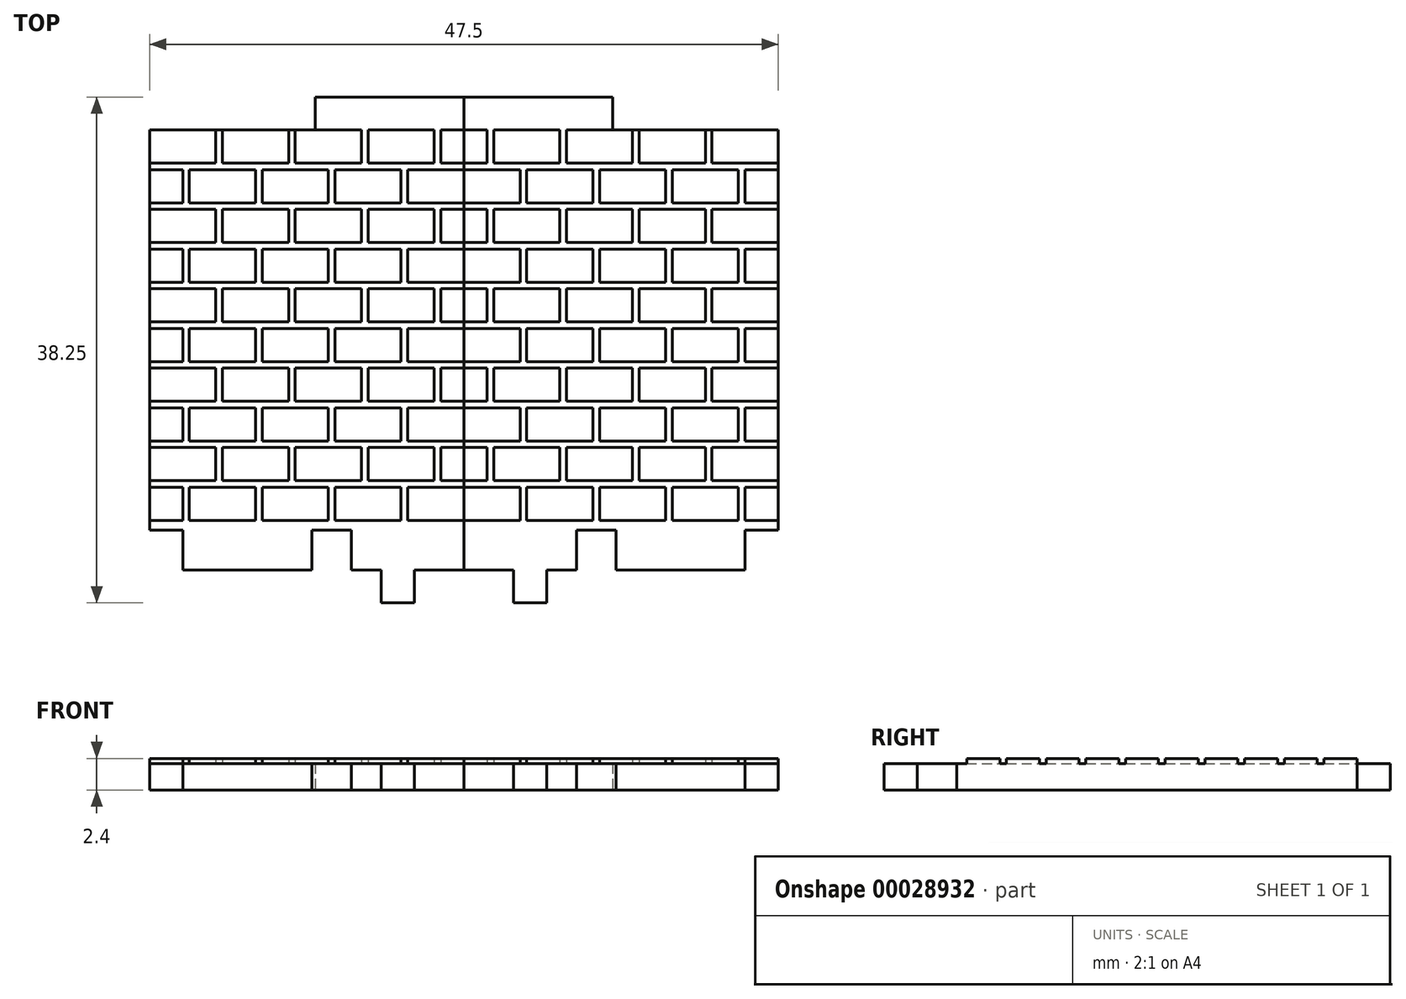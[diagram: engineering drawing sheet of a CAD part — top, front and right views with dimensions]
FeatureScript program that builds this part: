
annotation { "Feature Type Name" : "Feature", "Feature Type Description" : "" }
export const myFeature = defineFeature(function(context is Context, id is Id, definition is map)
    precondition{}
    {
        {
            var Q0;
            Q0=qCreatedBy(makeId("Top.planeOp"),FACE);
            var sketch = newSketch(context, id + "F0", { "sketchPlane" : qUnion([Q0])});
            skLineSegment(sketch, "E0.bottom", {"start": v(-8.5, -5.78) * mm, "end": v(-11.5, -5.78) * mm});
            skLineSegment(sketch, "E0.top", {"start": v(-11.25, 24.47) * mm, "end": v(-23.75, 24.47) * mm});
            skLineSegment(sketch, "E0.right", {"start": v(-23.75, -5.78) * mm, "end": v(-23.75, 24.47) * mm});
            skLineSegment(sketch, "E1.top", {"start": v(-11.25, 26.97) * mm, "end": v(0, 26.97) * mm});
            skLineSegment(sketch, "E1.left", {"start": v(-11.25, 24.47) * mm, "end": v(-11.25, 26.97) * mm});
            skLineSegment(sketch, "E1.right", {"start": v(0, -8.78) * mm, "end": v(0, 26.97) * mm});
            skLineSegment(sketch, "E2.top", {"start": v(-21.25, -8.78) * mm, "end": v(-11.5, -8.78) * mm});
            skLineSegment(sketch, "E2.left", {"start": v(-21.25, -5.78) * mm, "end": v(-21.25, -8.78) * mm});
            skLineSegment(sketch, "E2.right", {"start": v(-11.5, -5.78) * mm, "end": v(-11.5, -8.78) * mm});
            skLineSegment(sketch, "E3.top", {"start": v(-8.5, -8.78) * mm, "end": v(-6.25, -8.78) * mm});
            skLineSegment(sketch, "E3.left", {"start": v(-8.5, -5.78) * mm, "end": v(-8.5, -8.78) * mm});
            skLineSegment(sketch, "E4.top", {"start": v(-6.25, -11.28) * mm, "end": v(-3.75, -11.28) * mm});
            skLineSegment(sketch, "E4.left", {"start": v(-6.25, -8.78) * mm, "end": v(-6.25, -11.28) * mm});
            skLineSegment(sketch, "E4.right", {"start": v(-3.75, -8.78) * mm, "end": v(-3.75, -11.28) * mm});
            skLineSegment(sketch, "E5.trimOffspring", {"start": v(-3.75, -8.78) * mm, "end": v(0, -8.78) * mm});
            skLineSegment(sketch, "E6.trimOffspring", {"start": v(-21.25, -5.78) * mm, "end": v(-23.75, -5.78) * mm});
            skLineSegment(sketch, "E7.MirrorCS", {"start": v(11.25, 26.97) * mm, "end": v(0, 26.97) * mm});
            skLineSegment(sketch, "E8.MirrorCS", {"start": v(11.25, 24.47) * mm, "end": v(11.25, 26.97) * mm});
            skLineSegment(sketch, "E9.MirrorCS", {"start": v(11.25, 24.47) * mm, "end": v(23.75, 24.47) * mm});
            skLineSegment(sketch, "E10.MirrorCS", {"start": v(23.75, -5.78) * mm, "end": v(23.75, 24.47) * mm});
            skLineSegment(sketch, "E11.MirrorCS", {"start": v(21.25, -5.78) * mm, "end": v(23.75, -5.78) * mm});
            skLineSegment(sketch, "E12.MirrorCS", {"start": v(21.25, -5.78) * mm, "end": v(21.25, -8.78) * mm});
            skLineSegment(sketch, "E13.MirrorCS", {"start": v(21.25, -8.78) * mm, "end": v(11.5, -8.78) * mm});
            skLineSegment(sketch, "E14.MirrorCS", {"start": v(11.5, -5.78) * mm, "end": v(11.5, -8.78) * mm});
            skLineSegment(sketch, "E15.MirrorCS", {"start": v(8.5, -5.78) * mm, "end": v(11.5, -5.78) * mm});
            skLineSegment(sketch, "E16.MirrorCS", {"start": v(8.5, -5.78) * mm, "end": v(8.5, -8.78) * mm});
            skLineSegment(sketch, "E17.MirrorCS", {"start": v(8.5, -8.78) * mm, "end": v(6.25, -8.78) * mm});
            skLineSegment(sketch, "E18.MirrorCS", {"start": v(6.25, -8.78) * mm, "end": v(6.25, -11.28) * mm});
            skLineSegment(sketch, "E19.MirrorCS", {"start": v(6.25, -11.28) * mm, "end": v(3.75, -11.28) * mm});
            skLineSegment(sketch, "E20.MirrorCS", {"start": v(3.75, -8.78) * mm, "end": v(3.75, -11.28) * mm});
            skLineSegment(sketch, "E21.MirrorCS", {"start": v(3.75, -8.78) * mm, "end": v(0, -8.78) * mm});
            skSolve(sketch);
        }
        {
            var Q0;
            Q0=makeQuery(id+"F0.imprint","IMPRINT",FACE,{"disambiguationData":[TD([[makeQuery(id+"F0.imprint","IMPRINT",EDGE,{"derivedFrom":sQuery(id+"F0.wireOp",EDGE,"E0.bottom")}),-1.0]])]});
            extrude(context, id + "F1", {"entities" : qUnion([Q0]), "depth" : 2 * mm});
        }
        {
            var Q0;
            Q0=makeQuery(id+"F1.opExtrude","CAP_FACE",FACE,{"disambiguationData":[OSD([sQuery(id+"F0.wireOp",EDGE,"E0.bottom"),sQuery(id+"F0.wireOp",EDGE,"E0.top"),sQuery(id+"F0.wireOp",EDGE,"E0.right"),sQuery(id+"F0.wireOp",EDGE,"E1.top"),sQuery(id+"F0.wireOp",EDGE,"E1.left"),sQuery(id+"F0.wireOp",EDGE,"E1.right"),sQuery(id+"F0.wireOp",EDGE,"E2.top"),sQuery(id+"F0.wireOp",EDGE,"E2.left"),sQuery(id+"F0.wireOp",EDGE,"E2.right"),sQuery(id+"F0.wireOp",EDGE,"E3.top"),sQuery(id+"F0.wireOp",EDGE,"E3.left"),sQuery(id+"F0.wireOp",EDGE,"E4.top"),sQuery(id+"F0.wireOp",EDGE,"E4.left"),sQuery(id+"F0.wireOp",EDGE,"E4.right"),sQuery(id+"F0.wireOp",EDGE,"E5.trimOffspring"),sQuery(id+"F0.wireOp",EDGE,"E6.trimOffspring")])],"isStart":false});
            var sketch = newSketch(context, id + "F2", { "sketchPlane" : qUnion([Q0])});
            skLineSegment(sketch, "E22", {"start": v(-23.75, 21.97) * mm, "end": v(0, 21.97) * mm});
            skLineSegment(sketch, "E23", {"start": v(-23.75, 24.47) * mm, "end": v(0, 24.47) * mm});
            skLineSegment(sketch, "E24", {"start": v(-18.75, 24.47) * mm, "end": v(-18.75, 21.97) * mm});
            skLineSegment(sketch, "E25", {"start": v(-18.25, 21.97) * mm, "end": v(-18.25, 24.47) * mm});
            skLineSegment(sketch, "E26.1.0.0", {"start": v(-13.25, 24.47) * mm, "end": v(-13.25, 21.97) * mm});
            skLineSegment(sketch, "E26.1.0.1", {"start": v(-12.75, 21.97) * mm, "end": v(-12.75, 24.47) * mm});
            skLineSegment(sketch, "E26.2.0.0", {"start": v(-7.75, 24.47) * mm, "end": v(-7.75, 21.97) * mm});
            skLineSegment(sketch, "E26.2.0.1", {"start": v(-7.25, 21.97) * mm, "end": v(-7.25, 24.47) * mm});
            skLineSegment(sketch, "E26.3.0.0", {"start": v(-2.25, 24.47) * mm, "end": v(-2.25, 21.97) * mm});
            skLineSegment(sketch, "E26.3.0.1", {"start": v(-1.75, 21.97) * mm, "end": v(-1.75, 24.47) * mm});
            skLineSegment(sketch, "E26.direction1", {"start": v(-18.75, 21.97) * mm, "end": v(-13.25, 21.97) * mm, "construction": true});
            skLineSegment(sketch, "E27", {"start": v(0, 24.47) * mm, "end": v(4, 24.47) * mm});
            skLineSegment(sketch, "E28", {"start": v(0, 21.97) * mm, "end": v(4, 21.97) * mm});
            skLineSegment(sketch, "E29.1.0.0", {"start": v(-26.25, 21.47) * mm, "end": v(-2.5, 21.47) * mm});
            skLineSegment(sketch, "E29.1.0.1", {"start": v(-2.5, 21.47) * mm, "end": v(1.5, 21.47) * mm});
            skLineSegment(sketch, "E29.1.0.2", {"start": v(-2.5, 18.97) * mm, "end": v(1.5, 18.97) * mm});
            skLineSegment(sketch, "E29.1.0.3", {"start": v(-26.25, 18.97) * mm, "end": v(-2.5, 18.97) * mm});
            skLineSegment(sketch, "E29.1.0.4", {"start": v(-4.25, 18.97) * mm, "end": v(-4.25, 21.47) * mm});
            skLineSegment(sketch, "E29.1.0.5", {"start": v(-4.75, 21.47) * mm, "end": v(-4.75, 18.97) * mm});
            skLineSegment(sketch, "E29.1.0.6", {"start": v(-9.75, 18.97) * mm, "end": v(-9.75, 21.47) * mm});
            skLineSegment(sketch, "E29.1.0.7", {"start": v(-10.25, 21.47) * mm, "end": v(-10.25, 18.97) * mm});
            skLineSegment(sketch, "E29.1.0.8", {"start": v(-15.25, 18.97) * mm, "end": v(-15.25, 21.47) * mm});
            skLineSegment(sketch, "E29.1.0.9", {"start": v(-15.75, 21.47) * mm, "end": v(-15.75, 18.97) * mm});
            skLineSegment(sketch, "E29.1.0.10", {"start": v(-20.75, 18.97) * mm, "end": v(-20.75, 21.47) * mm});
            skLineSegment(sketch, "E29.1.0.11", {"start": v(-21.25, 21.47) * mm, "end": v(-21.25, 18.97) * mm});
            skLineSegment(sketch, "E29.direction1", {"start": v(-23.75, 24.47) * mm, "end": v(-26.25, 21.47) * mm, "construction": true});
            skLineSegment(sketch, "E30.0.1.0", {"start": v(-23.75, 18.47) * mm, "end": v(-26.25, 15.47) * mm, "construction": true});
            skLineSegment(sketch, "E30.0.1.1", {"start": v(-26.25, 12.97) * mm, "end": v(-2.5, 12.97) * mm});
            skLineSegment(sketch, "E30.0.1.2", {"start": v(-23.75, 18.47) * mm, "end": v(0, 18.47) * mm});
            skLineSegment(sketch, "E30.0.1.3", {"start": v(-2.5, 12.97) * mm, "end": v(1.5, 12.97) * mm});
            skLineSegment(sketch, "E30.0.1.4", {"start": v(-23.75, 15.97) * mm, "end": v(0, 15.97) * mm});
            skLineSegment(sketch, "E30.0.1.5", {"start": v(-26.25, 15.47) * mm, "end": v(-2.5, 15.47) * mm});
            skLineSegment(sketch, "E30.0.1.6", {"start": v(-13.25, 18.47) * mm, "end": v(-13.25, 15.97) * mm});
            skLineSegment(sketch, "E30.0.1.7", {"start": v(-4.25, 12.97) * mm, "end": v(-4.25, 15.47) * mm});
            skLineSegment(sketch, "E30.0.1.8", {"start": v(-1.75, 15.97) * mm, "end": v(-1.75, 18.47) * mm});
            skLineSegment(sketch, "E30.0.1.9", {"start": v(-4.75, 15.47) * mm, "end": v(-4.75, 12.97) * mm});
            skLineSegment(sketch, "E30.0.1.10", {"start": v(-7.25, 15.97) * mm, "end": v(-7.25, 18.47) * mm});
            skLineSegment(sketch, "E30.0.1.11", {"start": v(0, 15.97) * mm, "end": v(4, 15.97) * mm});
            skLineSegment(sketch, "E30.0.1.12", {"start": v(-9.75, 12.97) * mm, "end": v(-9.75, 15.47) * mm});
            skLineSegment(sketch, "E30.0.1.13", {"start": v(-15.75, 15.47) * mm, "end": v(-15.75, 12.97) * mm});
            skLineSegment(sketch, "E30.0.1.14", {"start": v(-10.25, 15.47) * mm, "end": v(-10.25, 12.97) * mm});
            skLineSegment(sketch, "E30.0.1.15", {"start": v(-2.25, 18.47) * mm, "end": v(-2.25, 15.97) * mm});
            skLineSegment(sketch, "E30.0.1.16", {"start": v(-20.75, 12.97) * mm, "end": v(-20.75, 15.47) * mm});
            skLineSegment(sketch, "E30.0.1.17", {"start": v(-18.75, 15.97) * mm, "end": v(-13.25, 15.97) * mm, "construction": true});
            skLineSegment(sketch, "E30.0.1.18", {"start": v(0, 18.47) * mm, "end": v(4, 18.47) * mm});
            skLineSegment(sketch, "E30.0.1.19", {"start": v(-7.75, 18.47) * mm, "end": v(-7.75, 15.97) * mm});
            skLineSegment(sketch, "E30.0.1.20", {"start": v(-18.75, 18.47) * mm, "end": v(-18.75, 15.97) * mm});
            skLineSegment(sketch, "E30.0.1.21", {"start": v(-18.25, 15.97) * mm, "end": v(-18.25, 18.47) * mm});
            skLineSegment(sketch, "E30.0.1.22", {"start": v(-21.25, 15.47) * mm, "end": v(-21.25, 12.97) * mm});
            skLineSegment(sketch, "E30.0.1.23", {"start": v(-12.75, 15.97) * mm, "end": v(-12.75, 18.47) * mm});
            skLineSegment(sketch, "E30.0.1.24", {"start": v(-15.25, 12.97) * mm, "end": v(-15.25, 15.47) * mm});
            skLineSegment(sketch, "E30.0.1.25", {"start": v(-2.5, 15.47) * mm, "end": v(1.5, 15.47) * mm});
            skLineSegment(sketch, "E30.direction1", {"start": v(-26.25, 21.47) * mm, "end": v(-1.25, 21.47) * mm, "construction": true});
            skLineSegment(sketch, "E30.direction2", {"start": v(-26.25, 21.47) * mm, "end": v(-26.25, 15.47) * mm, "construction": true});
            skLineSegment(sketch, "E31.0.0.2", {"start": v(-23.75, 12.47) * mm, "end": v(-26.25, 9.47) * mm, "construction": true});
            skLineSegment(sketch, "E31.3.0.2", {"start": v(-26.25, 6.97) * mm, "end": v(-2.5, 6.97) * mm});
            skLineSegment(sketch, "E31.6.0.2", {"start": v(-23.75, 12.47) * mm, "end": v(0, 12.47) * mm});
            skLineSegment(sketch, "E31.9.0.2", {"start": v(-2.5, 6.97) * mm, "end": v(1.5, 6.97) * mm});
            skLineSegment(sketch, "E31.12.0.2", {"start": v(-23.75, 9.97) * mm, "end": v(0, 9.97) * mm});
            skLineSegment(sketch, "E31.15.0.2", {"start": v(-26.25, 9.47) * mm, "end": v(-2.5, 9.47) * mm});
            skLineSegment(sketch, "E31.18.0.2", {"start": v(-13.25, 12.47) * mm, "end": v(-13.25, 9.97) * mm});
            skLineSegment(sketch, "E31.21.0.2", {"start": v(-4.25, 6.97) * mm, "end": v(-4.25, 9.47) * mm});
            skLineSegment(sketch, "E31.24.0.2", {"start": v(-1.75, 9.97) * mm, "end": v(-1.75, 12.47) * mm});
            skLineSegment(sketch, "E31.27.0.2", {"start": v(-4.75, 9.47) * mm, "end": v(-4.75, 6.97) * mm});
            skLineSegment(sketch, "E31.30.0.2", {"start": v(-7.25, 9.97) * mm, "end": v(-7.25, 12.47) * mm});
            skLineSegment(sketch, "E31.33.0.2", {"start": v(0, 9.97) * mm, "end": v(4, 9.97) * mm});
            skLineSegment(sketch, "E31.36.0.2", {"start": v(-9.75, 6.97) * mm, "end": v(-9.75, 9.47) * mm});
            skLineSegment(sketch, "E31.39.0.2", {"start": v(-15.75, 9.47) * mm, "end": v(-15.75, 6.97) * mm});
            skLineSegment(sketch, "E31.42.0.2", {"start": v(-10.25, 9.47) * mm, "end": v(-10.25, 6.97) * mm});
            skLineSegment(sketch, "E31.45.0.2", {"start": v(-2.25, 12.47) * mm, "end": v(-2.25, 9.97) * mm});
            skLineSegment(sketch, "E31.48.0.2", {"start": v(-20.75, 6.97) * mm, "end": v(-20.75, 9.47) * mm});
            skLineSegment(sketch, "E31.51.0.2", {"start": v(-18.75, 9.97) * mm, "end": v(-13.25, 9.97) * mm, "construction": true});
            skLineSegment(sketch, "E31.54.0.2", {"start": v(0, 12.47) * mm, "end": v(4, 12.47) * mm});
            skLineSegment(sketch, "E31.57.0.2", {"start": v(-7.75, 12.47) * mm, "end": v(-7.75, 9.97) * mm});
            skLineSegment(sketch, "E31.60.0.2", {"start": v(-18.75, 12.47) * mm, "end": v(-18.75, 9.97) * mm});
            skLineSegment(sketch, "E31.63.0.2", {"start": v(-18.25, 9.97) * mm, "end": v(-18.25, 12.47) * mm});
            skLineSegment(sketch, "E31.66.0.2", {"start": v(-21.25, 9.47) * mm, "end": v(-21.25, 6.97) * mm});
            skLineSegment(sketch, "E31.69.0.2", {"start": v(-12.75, 9.97) * mm, "end": v(-12.75, 12.47) * mm});
            skLineSegment(sketch, "E31.72.0.2", {"start": v(-15.25, 6.97) * mm, "end": v(-15.25, 9.47) * mm});
            skLineSegment(sketch, "E31.75.0.2", {"start": v(-2.5, 9.47) * mm, "end": v(1.5, 9.47) * mm});
            skLineSegment(sketch, "E32.0.0.3", {"start": v(-23.75, 6.47) * mm, "end": v(-26.25, 3.47) * mm, "construction": true});
            skLineSegment(sketch, "E32.3.0.3", {"start": v(-26.25, 0.97) * mm, "end": v(-2.5, 0.97) * mm});
            skLineSegment(sketch, "E32.6.0.3", {"start": v(-23.75, 6.47) * mm, "end": v(0, 6.47) * mm});
            skLineSegment(sketch, "E32.9.0.3", {"start": v(-2.5, 0.97) * mm, "end": v(1.5, 0.97) * mm});
            skLineSegment(sketch, "E32.12.0.3", {"start": v(-23.75, 3.97) * mm, "end": v(0, 3.97) * mm});
            skLineSegment(sketch, "E32.15.0.3", {"start": v(-26.25, 3.47) * mm, "end": v(-2.5, 3.47) * mm});
            skLineSegment(sketch, "E32.18.0.3", {"start": v(-13.25, 6.47) * mm, "end": v(-13.25, 3.97) * mm});
            skLineSegment(sketch, "E32.21.0.3", {"start": v(-4.25, 0.97) * mm, "end": v(-4.25, 3.47) * mm});
            skLineSegment(sketch, "E32.24.0.3", {"start": v(-1.75, 3.97) * mm, "end": v(-1.75, 6.47) * mm});
            skLineSegment(sketch, "E32.27.0.3", {"start": v(-4.75, 3.47) * mm, "end": v(-4.75, 0.97) * mm});
            skLineSegment(sketch, "E32.30.0.3", {"start": v(-7.25, 3.97) * mm, "end": v(-7.25, 6.47) * mm});
            skLineSegment(sketch, "E32.33.0.3", {"start": v(0, 3.97) * mm, "end": v(4, 3.97) * mm});
            skLineSegment(sketch, "E32.36.0.3", {"start": v(-9.75, 0.97) * mm, "end": v(-9.75, 3.47) * mm});
            skLineSegment(sketch, "E32.39.0.3", {"start": v(-15.75, 3.47) * mm, "end": v(-15.75, 0.97) * mm});
            skLineSegment(sketch, "E32.42.0.3", {"start": v(-10.25, 3.47) * mm, "end": v(-10.25, 0.97) * mm});
            skLineSegment(sketch, "E32.45.0.3", {"start": v(-2.25, 6.47) * mm, "end": v(-2.25, 3.97) * mm});
            skLineSegment(sketch, "E32.48.0.3", {"start": v(-20.75, 0.97) * mm, "end": v(-20.75, 3.47) * mm});
            skLineSegment(sketch, "E32.51.0.3", {"start": v(-18.75, 3.97) * mm, "end": v(-13.25, 3.97) * mm, "construction": true});
            skLineSegment(sketch, "E32.54.0.3", {"start": v(0, 6.47) * mm, "end": v(4, 6.47) * mm});
            skLineSegment(sketch, "E32.57.0.3", {"start": v(-7.75, 6.47) * mm, "end": v(-7.75, 3.97) * mm});
            skLineSegment(sketch, "E32.60.0.3", {"start": v(-18.75, 6.47) * mm, "end": v(-18.75, 3.97) * mm});
            skLineSegment(sketch, "E32.63.0.3", {"start": v(-18.25, 3.97) * mm, "end": v(-18.25, 6.47) * mm});
            skLineSegment(sketch, "E32.66.0.3", {"start": v(-21.25, 3.47) * mm, "end": v(-21.25, 0.97) * mm});
            skLineSegment(sketch, "E32.69.0.3", {"start": v(-12.75, 3.97) * mm, "end": v(-12.75, 6.47) * mm});
            skLineSegment(sketch, "E32.72.0.3", {"start": v(-15.25, 0.97) * mm, "end": v(-15.25, 3.47) * mm});
            skLineSegment(sketch, "E32.75.0.3", {"start": v(-2.5, 3.47) * mm, "end": v(1.5, 3.47) * mm});
            skLineSegment(sketch, "E32.0.0.4", {"start": v(-23.75, 0.47) * mm, "end": v(-26.25, -2.53) * mm, "construction": true});
            skLineSegment(sketch, "E32.3.0.4", {"start": v(-26.25, -5.03) * mm, "end": v(-2.5, -5.03) * mm});
            skLineSegment(sketch, "E32.6.0.4", {"start": v(-23.75, 0.47) * mm, "end": v(0, 0.47) * mm});
            skLineSegment(sketch, "E32.9.0.4", {"start": v(-2.5, -5.03) * mm, "end": v(1.5, -5.03) * mm});
            skLineSegment(sketch, "E32.12.0.4", {"start": v(-23.75, -2.03) * mm, "end": v(0, -2.03) * mm});
            skLineSegment(sketch, "E32.15.0.4", {"start": v(-26.25, -2.53) * mm, "end": v(-2.5, -2.53) * mm});
            skLineSegment(sketch, "E32.18.0.4", {"start": v(-13.25, 0.47) * mm, "end": v(-13.25, -2.03) * mm});
            skLineSegment(sketch, "E32.21.0.4", {"start": v(-4.25, -5.03) * mm, "end": v(-4.25, -2.53) * mm});
            skLineSegment(sketch, "E32.24.0.4", {"start": v(-1.75, -2.03) * mm, "end": v(-1.75, 0.47) * mm});
            skLineSegment(sketch, "E32.27.0.4", {"start": v(-4.75, -2.53) * mm, "end": v(-4.75, -5.03) * mm});
            skLineSegment(sketch, "E32.30.0.4", {"start": v(-7.25, -2.03) * mm, "end": v(-7.25, 0.47) * mm});
            skLineSegment(sketch, "E32.33.0.4", {"start": v(0, -2.03) * mm, "end": v(4, -2.03) * mm});
            skLineSegment(sketch, "E32.36.0.4", {"start": v(-9.75, -5.03) * mm, "end": v(-9.75, -2.53) * mm});
            skLineSegment(sketch, "E32.39.0.4", {"start": v(-15.75, -2.53) * mm, "end": v(-15.75, -5.03) * mm});
            skLineSegment(sketch, "E32.42.0.4", {"start": v(-10.25, -2.53) * mm, "end": v(-10.25, -5.03) * mm});
            skLineSegment(sketch, "E32.45.0.4", {"start": v(-2.25, 0.47) * mm, "end": v(-2.25, -2.03) * mm});
            skLineSegment(sketch, "E32.48.0.4", {"start": v(-20.75, -5.03) * mm, "end": v(-20.75, -2.53) * mm});
            skLineSegment(sketch, "E32.51.0.4", {"start": v(-18.75, -2.03) * mm, "end": v(-13.25, -2.03) * mm, "construction": true});
            skLineSegment(sketch, "E32.54.0.4", {"start": v(0, 0.47) * mm, "end": v(4, 0.47) * mm});
            skLineSegment(sketch, "E32.57.0.4", {"start": v(-7.75, 0.47) * mm, "end": v(-7.75, -2.03) * mm});
            skLineSegment(sketch, "E32.60.0.4", {"start": v(-18.75, 0.47) * mm, "end": v(-18.75, -2.03) * mm});
            skLineSegment(sketch, "E32.63.0.4", {"start": v(-18.25, -2.03) * mm, "end": v(-18.25, 0.47) * mm});
            skLineSegment(sketch, "E32.66.0.4", {"start": v(-21.25, -2.53) * mm, "end": v(-21.25, -5.03) * mm});
            skLineSegment(sketch, "E32.69.0.4", {"start": v(-12.75, -2.03) * mm, "end": v(-12.75, 0.47) * mm});
            skLineSegment(sketch, "E32.72.0.4", {"start": v(-15.25, -5.03) * mm, "end": v(-15.25, -2.53) * mm});
            skLineSegment(sketch, "E32.75.0.4", {"start": v(-2.5, -2.53) * mm, "end": v(1.5, -2.53) * mm});
            skSolve(sketch);
        }
        {
            var Q0;
            {var subQ5=sQuery(id+"F2.wireOp",EDGE,"E24");Q0=makeQuery(id+"F2.imprint","IMPRINT",FACE,{"disambiguationData":[TD([[makeQuery(id+"F2.imprint","IMPRINT",EDGE,{"derivedFrom":subQ5}),-1.0]])]});}
            var Q1;
            {var subQ1=sQuery(id+"F2.wireOp",EDGE,"E25");Q1=makeQuery(id+"F2.imprint","IMPRINT",FACE,{"disambiguationData":[TD([[makeQuery(id+"F2.imprint","IMPRINT",EDGE,{"derivedFrom":subQ1}),-1.0]])]});}
            var Q2;
            {var subQ1=sQuery(id+"F2.wireOp",EDGE,"E26.1.0.1");Q2=makeQuery(id+"F2.imprint","IMPRINT",FACE,{"disambiguationData":[TD([[makeQuery(id+"F2.imprint","IMPRINT",EDGE,{"derivedFrom":subQ1}),-1.0]])]});}
            var Q3;
            {var subQ0=sQuery(id+"F2.wireOp",EDGE,"E26.2.0.1");Q3=makeQuery(id+"F2.imprint","IMPRINT",FACE,{"disambiguationData":[TD([[makeQuery(id+"F2.imprint","IMPRINT",EDGE,{"derivedFrom":subQ0}),-1.0]])]});}
            var Q4;
            {var subQ5=sQuery(id+"F2.wireOp",EDGE,"E26.3.0.1");Q4=makeQuery(id+"F2.imprint","IMPRINT",FACE,{"disambiguationData":[TD([[makeQuery(id+"F2.imprint","IMPRINT",EDGE,{"derivedFrom":subQ5}),-1.0]])]});}
            var Q5;
            {var subQ5=sQuery(id+"F2.wireOp",EDGE,"E29.1.0.4");Q5=makeQuery(id+"F2.imprint","IMPRINT",FACE,{"disambiguationData":[TD([[makeQuery(id+"F2.imprint","IMPRINT",EDGE,{"derivedFrom":subQ5}),-1.0]])]});}
            var Q6;
            {var subQ1=sQuery(id+"F2.wireOp",EDGE,"E29.1.0.5");Q6=makeQuery(id+"F2.imprint","IMPRINT",FACE,{"disambiguationData":[TD([[makeQuery(id+"F2.imprint","IMPRINT",EDGE,{"derivedFrom":subQ1}),-1.0]])]});}
            var Q7;
            {var subQ1=sQuery(id+"F2.wireOp",EDGE,"E29.1.0.7");Q7=makeQuery(id+"F2.imprint","IMPRINT",FACE,{"disambiguationData":[TD([[makeQuery(id+"F2.imprint","IMPRINT",EDGE,{"derivedFrom":subQ1}),-1.0]])]});}
            var Q8;
            {var subQ1=sQuery(id+"F2.wireOp",EDGE,"E29.1.0.9");Q8=makeQuery(id+"F2.imprint","IMPRINT",FACE,{"disambiguationData":[TD([[makeQuery(id+"F2.imprint","IMPRINT",EDGE,{"derivedFrom":subQ1}),-1.0]])]});}
            var Q9;
            {var subQ5=sQuery(id+"F2.wireOp",EDGE,"E29.1.0.11");Q9=makeQuery(id+"F2.imprint","IMPRINT",FACE,{"disambiguationData":[TD([[makeQuery(id+"F2.imprint","IMPRINT",EDGE,{"derivedFrom":subQ5}),-1.0]])]});}
            var Q10;
            {var subQ5=sQuery(id+"F2.wireOp",EDGE,"E30.0.1.20");Q10=makeQuery(id+"F2.imprint","IMPRINT",FACE,{"disambiguationData":[TD([[makeQuery(id+"F2.imprint","IMPRINT",EDGE,{"derivedFrom":subQ5}),-1.0]])]});}
            var Q11;
            {var subQ1=sQuery(id+"F2.wireOp",EDGE,"E30.0.1.6");Q11=makeQuery(id+"F2.imprint","IMPRINT",FACE,{"disambiguationData":[TD([[makeQuery(id+"F2.imprint","IMPRINT",EDGE,{"derivedFrom":subQ1}),-1.0]])]});}
            var Q12;
            {var subQ1=sQuery(id+"F2.wireOp",EDGE,"E30.0.1.19");Q12=makeQuery(id+"F2.imprint","IMPRINT",FACE,{"disambiguationData":[TD([[makeQuery(id+"F2.imprint","IMPRINT",EDGE,{"derivedFrom":subQ1}),-1.0]])]});}
            var Q13;
            {var subQ1=sQuery(id+"F2.wireOp",EDGE,"E30.0.1.10");Q13=makeQuery(id+"F2.imprint","IMPRINT",FACE,{"disambiguationData":[TD([[makeQuery(id+"F2.imprint","IMPRINT",EDGE,{"derivedFrom":subQ1}),-1.0]])]});}
            var Q14;
            {var subQ5=sQuery(id+"F2.wireOp",EDGE,"E30.0.1.8");Q14=makeQuery(id+"F2.imprint","IMPRINT",FACE,{"disambiguationData":[TD([[makeQuery(id+"F2.imprint","IMPRINT",EDGE,{"derivedFrom":subQ5}),-1.0]])]});}
            var Q15;
            {var subQ7=sQuery(id+"F2.wireOp",EDGE,"E30.0.1.7");Q15=makeQuery(id+"F2.imprint","IMPRINT",FACE,{"disambiguationData":[TD([[makeQuery(id+"F2.imprint","IMPRINT",EDGE,{"derivedFrom":subQ7}),-1.0]])]});}
            var Q16;
            {var subQ1=sQuery(id+"F2.wireOp",EDGE,"E30.0.1.9");Q16=makeQuery(id+"F2.imprint","IMPRINT",FACE,{"disambiguationData":[TD([[makeQuery(id+"F2.imprint","IMPRINT",EDGE,{"derivedFrom":subQ1}),-1.0]])]});}
            var Q17;
            {var subQ1=sQuery(id+"F2.wireOp",EDGE,"E30.0.1.14");Q17=makeQuery(id+"F2.imprint","IMPRINT",FACE,{"disambiguationData":[TD([[makeQuery(id+"F2.imprint","IMPRINT",EDGE,{"derivedFrom":subQ1}),-1.0]])]});}
            var Q18;
            {var subQ1=sQuery(id+"F2.wireOp",EDGE,"E30.0.1.13");Q18=makeQuery(id+"F2.imprint","IMPRINT",FACE,{"disambiguationData":[TD([[makeQuery(id+"F2.imprint","IMPRINT",EDGE,{"derivedFrom":subQ1}),-1.0]])]});}
            var Q19;
            {var subQ5=sQuery(id+"F2.wireOp",EDGE,"E30.0.1.22");Q19=makeQuery(id+"F2.imprint","IMPRINT",FACE,{"disambiguationData":[TD([[makeQuery(id+"F2.imprint","IMPRINT",EDGE,{"derivedFrom":subQ5}),-1.0]])]});}
            var Q20;
            {var subQ5=sQuery(id+"F2.wireOp",EDGE,"E31.60.0.2");Q20=makeQuery(id+"F2.imprint","IMPRINT",FACE,{"disambiguationData":[TD([[makeQuery(id+"F2.imprint","IMPRINT",EDGE,{"derivedFrom":subQ5}),-1.0]])]});}
            var Q21;
            {var subQ0=sQuery(id+"F2.wireOp",EDGE,"E31.18.0.2");Q21=makeQuery(id+"F2.imprint","IMPRINT",FACE,{"disambiguationData":[TD([[makeQuery(id+"F2.imprint","IMPRINT",EDGE,{"derivedFrom":subQ0}),-1.0]])]});}
            var Q22;
            {var subQ0=sQuery(id+"F2.wireOp",EDGE,"E31.57.0.2");Q22=makeQuery(id+"F2.imprint","IMPRINT",FACE,{"disambiguationData":[TD([[makeQuery(id+"F2.imprint","IMPRINT",EDGE,{"derivedFrom":subQ0}),-1.0]])]});}
            var Q23;
            {var subQ1=sQuery(id+"F2.wireOp",EDGE,"E31.30.0.2");Q23=makeQuery(id+"F2.imprint","IMPRINT",FACE,{"disambiguationData":[TD([[makeQuery(id+"F2.imprint","IMPRINT",EDGE,{"derivedFrom":subQ1}),-1.0]])]});}
            var Q24;
            {var subQ5=sQuery(id+"F2.wireOp",EDGE,"E31.24.0.2");Q24=makeQuery(id+"F2.imprint","IMPRINT",FACE,{"disambiguationData":[TD([[makeQuery(id+"F2.imprint","IMPRINT",EDGE,{"derivedFrom":subQ5}),-1.0]])]});}
            var Q25;
            {var subQ7=sQuery(id+"F2.wireOp",EDGE,"E31.21.0.2");Q25=makeQuery(id+"F2.imprint","IMPRINT",FACE,{"disambiguationData":[TD([[makeQuery(id+"F2.imprint","IMPRINT",EDGE,{"derivedFrom":subQ7}),-1.0]])]});}
            var Q26;
            {var subQ1=sQuery(id+"F2.wireOp",EDGE,"E31.27.0.2");Q26=makeQuery(id+"F2.imprint","IMPRINT",FACE,{"disambiguationData":[TD([[makeQuery(id+"F2.imprint","IMPRINT",EDGE,{"derivedFrom":subQ1}),-1.0]])]});}
            var Q27;
            {var subQ1=sQuery(id+"F2.wireOp",EDGE,"E31.42.0.2");Q27=makeQuery(id+"F2.imprint","IMPRINT",FACE,{"disambiguationData":[TD([[makeQuery(id+"F2.imprint","IMPRINT",EDGE,{"derivedFrom":subQ1}),-1.0]])]});}
            var Q28;
            {var subQ1=sQuery(id+"F2.wireOp",EDGE,"E31.39.0.2");Q28=makeQuery(id+"F2.imprint","IMPRINT",FACE,{"disambiguationData":[TD([[makeQuery(id+"F2.imprint","IMPRINT",EDGE,{"derivedFrom":subQ1}),-1.0]])]});}
            var Q29;
            {var subQ5=sQuery(id+"F2.wireOp",EDGE,"E31.66.0.2");Q29=makeQuery(id+"F2.imprint","IMPRINT",FACE,{"disambiguationData":[TD([[makeQuery(id+"F2.imprint","IMPRINT",EDGE,{"derivedFrom":subQ5}),-1.0]])]});}
            var Q30;
            {var subQ5=sQuery(id+"F2.wireOp",EDGE,"E32.60.0.3");Q30=makeQuery(id+"F2.imprint","IMPRINT",FACE,{"disambiguationData":[TD([[makeQuery(id+"F2.imprint","IMPRINT",EDGE,{"derivedFrom":subQ5}),-1.0]])]});}
            var Q31;
            {var subQ1=sQuery(id+"F2.wireOp",EDGE,"E32.18.0.3");Q31=makeQuery(id+"F2.imprint","IMPRINT",FACE,{"disambiguationData":[TD([[makeQuery(id+"F2.imprint","IMPRINT",EDGE,{"derivedFrom":subQ1}),-1.0]])]});}
            var Q32;
            {var subQ1=sQuery(id+"F2.wireOp",EDGE,"E32.57.0.3");Q32=makeQuery(id+"F2.imprint","IMPRINT",FACE,{"disambiguationData":[TD([[makeQuery(id+"F2.imprint","IMPRINT",EDGE,{"derivedFrom":subQ1}),-1.0]])]});}
            var Q33;
            {var subQ0=sQuery(id+"F2.wireOp",EDGE,"E32.30.0.3");Q33=makeQuery(id+"F2.imprint","IMPRINT",FACE,{"disambiguationData":[TD([[makeQuery(id+"F2.imprint","IMPRINT",EDGE,{"derivedFrom":subQ0}),-1.0]])]});}
            var Q34;
            {var subQ5=sQuery(id+"F2.wireOp",EDGE,"E32.24.0.3");Q34=makeQuery(id+"F2.imprint","IMPRINT",FACE,{"disambiguationData":[TD([[makeQuery(id+"F2.imprint","IMPRINT",EDGE,{"derivedFrom":subQ5}),-1.0]])]});}
            var Q35;
            {var subQ1=sQuery(id+"F2.wireOp",EDGE,"E32.57.0.3");Q35=makeQuery(id+"F2.imprint","IMPRINT",FACE,{"disambiguationData":[TD([[makeQuery(id+"F2.imprint","IMPRINT",EDGE,{"derivedFrom":subQ1}),-1.0]])]});}
            var Q36;
            {var subQ1=sQuery(id+"F2.wireOp",EDGE,"E32.27.0.3");Q36=makeQuery(id+"F2.imprint","IMPRINT",FACE,{"disambiguationData":[TD([[makeQuery(id+"F2.imprint","IMPRINT",EDGE,{"derivedFrom":subQ1}),-1.0]])]});}
            var Q37;
            {var subQ5=sQuery(id+"F2.wireOp",EDGE,"E32.21.0.3");Q37=makeQuery(id+"F2.imprint","IMPRINT",FACE,{"disambiguationData":[TD([[makeQuery(id+"F2.imprint","IMPRINT",EDGE,{"derivedFrom":subQ5}),-1.0]])]});}
            var Q38;
            {var subQ1=sQuery(id+"F2.wireOp",EDGE,"E32.42.0.3");Q38=makeQuery(id+"F2.imprint","IMPRINT",FACE,{"disambiguationData":[TD([[makeQuery(id+"F2.imprint","IMPRINT",EDGE,{"derivedFrom":subQ1}),-1.0]])]});}
            var Q39;
            {var subQ1=sQuery(id+"F2.wireOp",EDGE,"E32.39.0.3");Q39=makeQuery(id+"F2.imprint","IMPRINT",FACE,{"disambiguationData":[TD([[makeQuery(id+"F2.imprint","IMPRINT",EDGE,{"derivedFrom":subQ1}),-1.0]])]});}
            var Q40;
            {var subQ5=sQuery(id+"F2.wireOp",EDGE,"E32.66.0.3");Q40=makeQuery(id+"F2.imprint","IMPRINT",FACE,{"disambiguationData":[TD([[makeQuery(id+"F2.imprint","IMPRINT",EDGE,{"derivedFrom":subQ5}),-1.0]])]});}
            var Q41;
            {var subQ5=sQuery(id+"F2.wireOp",EDGE,"E32.60.0.4");Q41=makeQuery(id+"F2.imprint","IMPRINT",FACE,{"disambiguationData":[TD([[makeQuery(id+"F2.imprint","IMPRINT",EDGE,{"derivedFrom":subQ5}),-1.0]])]});}
            var Q42;
            {var subQ1=sQuery(id+"F2.wireOp",EDGE,"E32.18.0.4");Q42=makeQuery(id+"F2.imprint","IMPRINT",FACE,{"disambiguationData":[TD([[makeQuery(id+"F2.imprint","IMPRINT",EDGE,{"derivedFrom":subQ1}),-1.0]])]});}
            var Q43;
            {var subQ1=sQuery(id+"F2.wireOp",EDGE,"E32.57.0.4");Q43=makeQuery(id+"F2.imprint","IMPRINT",FACE,{"disambiguationData":[TD([[makeQuery(id+"F2.imprint","IMPRINT",EDGE,{"derivedFrom":subQ1}),-1.0]])]});}
            var Q44;
            {var subQ1=sQuery(id+"F2.wireOp",EDGE,"E32.30.0.4");Q44=makeQuery(id+"F2.imprint","IMPRINT",FACE,{"disambiguationData":[TD([[makeQuery(id+"F2.imprint","IMPRINT",EDGE,{"derivedFrom":subQ1}),-1.0]])]});}
            var Q45;
            {var subQ5=sQuery(id+"F2.wireOp",EDGE,"E32.24.0.4");Q45=makeQuery(id+"F2.imprint","IMPRINT",FACE,{"disambiguationData":[TD([[makeQuery(id+"F2.imprint","IMPRINT",EDGE,{"derivedFrom":subQ5}),-1.0]])]});}
            var Q46;
            {var subQ5=sQuery(id+"F2.wireOp",EDGE,"E32.21.0.4");Q46=makeQuery(id+"F2.imprint","IMPRINT",FACE,{"disambiguationData":[TD([[makeQuery(id+"F2.imprint","IMPRINT",EDGE,{"derivedFrom":subQ5}),-1.0]])]});}
            var Q47;
            {var subQ1=sQuery(id+"F2.wireOp",EDGE,"E32.27.0.4");Q47=makeQuery(id+"F2.imprint","IMPRINT",FACE,{"disambiguationData":[TD([[makeQuery(id+"F2.imprint","IMPRINT",EDGE,{"derivedFrom":subQ1}),-1.0]])]});}
            var Q48;
            {var subQ0=sQuery(id+"F2.wireOp",EDGE,"E32.42.0.4");Q48=makeQuery(id+"F2.imprint","IMPRINT",FACE,{"disambiguationData":[TD([[makeQuery(id+"F2.imprint","IMPRINT",EDGE,{"derivedFrom":subQ0}),-1.0]])]});}
            var Q49;
            {var subQ1=sQuery(id+"F2.wireOp",EDGE,"E32.39.0.4");Q49=makeQuery(id+"F2.imprint","IMPRINT",FACE,{"disambiguationData":[TD([[makeQuery(id+"F2.imprint","IMPRINT",EDGE,{"derivedFrom":subQ1}),-1.0]])]});}
            var Q50;
            {var subQ5=sQuery(id+"F2.wireOp",EDGE,"E32.66.0.4");Q50=makeQuery(id+"F2.imprint","IMPRINT",FACE,{"disambiguationData":[TD([[makeQuery(id+"F2.imprint","IMPRINT",EDGE,{"derivedFrom":subQ5}),-1.0]])]});}
            extrude(context, id + "F3", {"entities" : qUnion([Q0, Q1, Q2, Q3, Q4, Q5, Q6, Q7, Q8, Q9, Q10, Q11, Q12, Q13, Q14, Q15, Q16, Q17, Q18, Q19, Q20, Q21, Q22, Q23, Q24, Q25, Q26, Q27, Q28, Q29, Q30, Q31, Q32, Q33, Q34, Q35, Q36, Q37, Q38, Q39, Q40, Q41, Q42, Q43, Q44, Q45, Q46, Q47, Q48, Q49, Q50]), "operationType" : NewBodyOperationType.ADD, "depth" : 0.4 * mm});
        }
        {
            var Q0;
            Q0=makeQuery(id+"F1.opExtrude","SWEPT_BODY",BODY,{"disambiguationData":[OSD([sQuery(id+"F0.wireOp",EDGE,"E0.bottom"),sQuery(id+"F0.wireOp",EDGE,"E0.top"),sQuery(id+"F0.wireOp",EDGE,"E0.right"),sQuery(id+"F0.wireOp",EDGE,"E1.top"),sQuery(id+"F0.wireOp",EDGE,"E1.left"),sQuery(id+"F0.wireOp",EDGE,"E1.right"),sQuery(id+"F0.wireOp",EDGE,"E2.top"),sQuery(id+"F0.wireOp",EDGE,"E2.left"),sQuery(id+"F0.wireOp",EDGE,"E2.right"),sQuery(id+"F0.wireOp",EDGE,"E3.top"),sQuery(id+"F0.wireOp",EDGE,"E3.left"),sQuery(id+"F0.wireOp",EDGE,"E4.top"),sQuery(id+"F0.wireOp",EDGE,"E4.left"),sQuery(id+"F0.wireOp",EDGE,"E4.right"),sQuery(id+"F0.wireOp",EDGE,"E5.trimOffspring"),sQuery(id+"F0.wireOp",EDGE,"E6.trimOffspring")])]});
            var Q1;
            Q1=qCreatedBy(makeId("Right.planeOp"),FACE);
            mirror(context, id + "F4", {"entities" : qUnion([Q0]), "mirrorPlane" : qUnion([Q1])});
        }
    });
